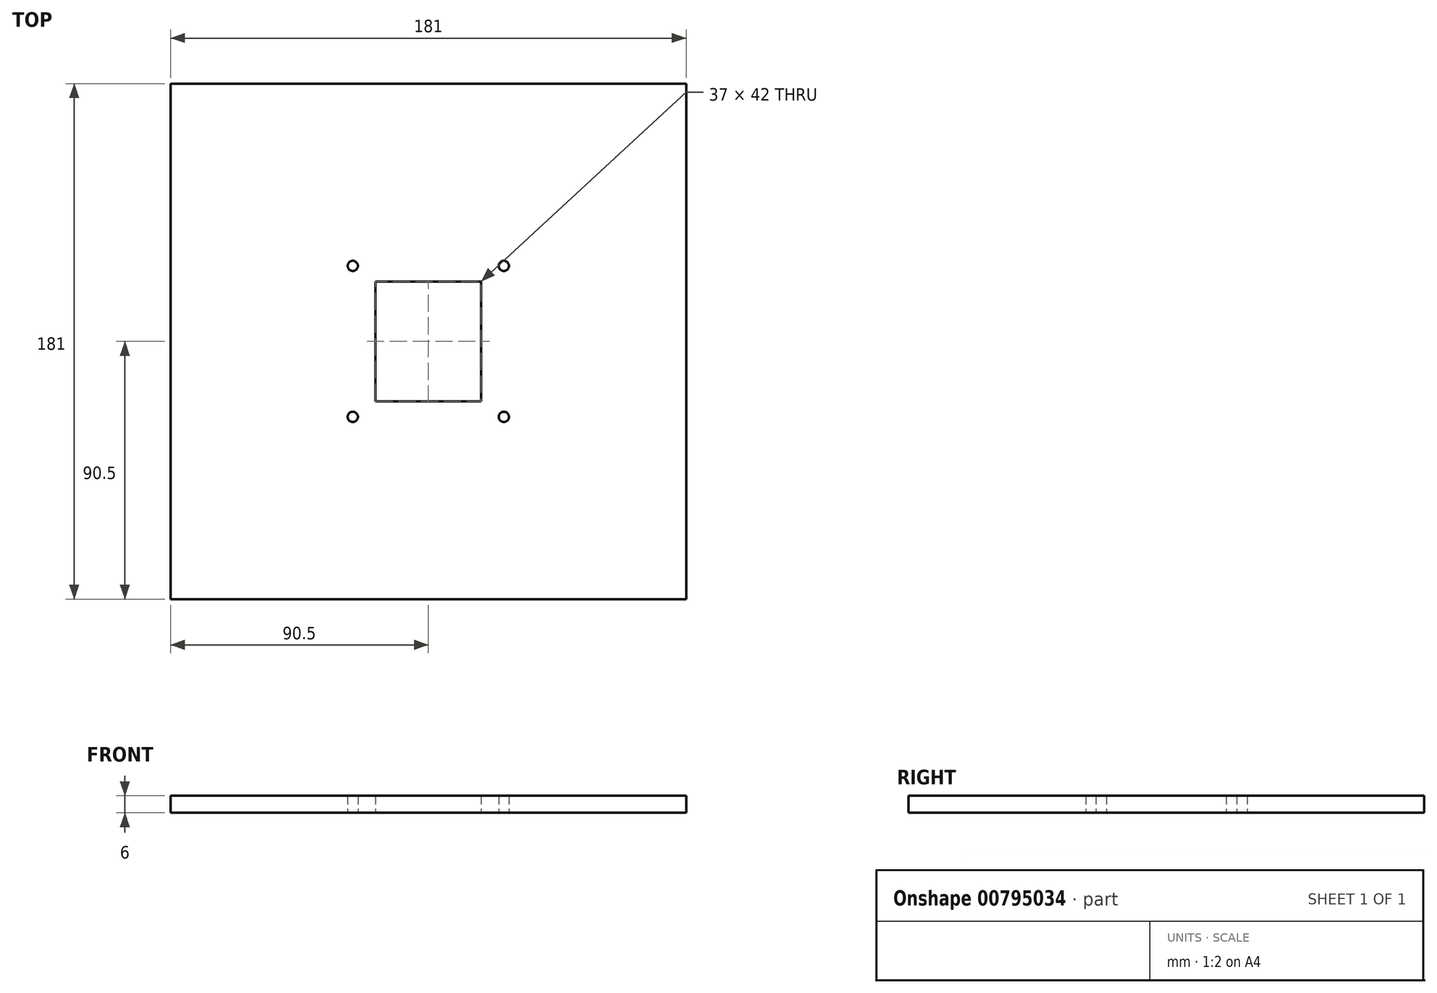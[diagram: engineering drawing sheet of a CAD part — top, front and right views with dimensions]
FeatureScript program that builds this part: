
annotation { "Feature Type Name" : "Feature", "Feature Type Description" : "" }
export const myFeature = defineFeature(function(context is Context, id is Id, definition is map)
    precondition{}
    {
        {
            var Q0;
            Q0=qCreatedBy(makeId("Top.planeOp"),FACE);
            var sketch = newSketch(context, id + "F0", { "sketchPlane" : qUnion([Q0])});
            skLineSegment(sketch, "E0.bottom", {"start": v(90.5, 90.5) * mm, "end": v(-90.5, 90.5) * mm});
            skLineSegment(sketch, "E0.top", {"start": v(90.5, -90.5) * mm, "end": v(-90.5, -90.5) * mm});
            skLineSegment(sketch, "E0.left", {"start": v(90.5, 90.5) * mm, "end": v(90.5, -90.5) * mm});
            skLineSegment(sketch, "E0.right", {"start": v(-90.5, 90.5) * mm, "end": v(-90.5, -90.5) * mm});
            skPoint(sketch, "E0.middle", {"position": v(0, 0) * mm});
            skLineSegment(sketch, "E1.bottom", {"start": v(-18.5, 21) * mm, "end": v(18.5, 21) * mm});
            skLineSegment(sketch, "E1.top", {"start": v(-18.5, -21) * mm, "end": v(18.5, -21) * mm});
            skLineSegment(sketch, "E1.left", {"start": v(-18.5, 21) * mm, "end": v(-18.5, -21) * mm});
            skLineSegment(sketch, "E1.right", {"start": v(18.5, 21) * mm, "end": v(18.5, -21) * mm});
            skCircle(sketch, "E2", {"center": v(-26.5, 26.5) * mm, "radius": 1.8 * mm});
            skCircle(sketch, "E3.0.1.0", {"center": v(-26.5, -26.5) * mm, "radius": 1.8 * mm});
            skCircle(sketch, "E3.1.0.0", {"center": v(26.5, 26.5) * mm, "radius": 1.8 * mm});
            skCircle(sketch, "E3.1.1.0", {"center": v(26.5, -26.5) * mm, "radius": 1.8 * mm});
            skLineSegment(sketch, "E3.direction1", {"start": v(-26.5, 26.5) * mm, "end": v(26.5, 26.5) * mm, "construction": true});
            skLineSegment(sketch, "E3.direction2", {"start": v(-26.5, 26.5) * mm, "end": v(-26.5, -26.5) * mm, "construction": true});
            skSolve(sketch);
        }
        {
            var Q0;
            Q0=makeQuery(id+"F0.imprint","IMPRINT",FACE,{"disambiguationData":[TD([[makeQuery(id+"F0.imprint","IMPRINT",EDGE,{"derivedFrom":sQuery(id+"F0.wireOp",EDGE,"E0.bottom")}),1.0]])]});
            extrude(context, id + "F1", {"entities" : qUnion([Q0]), "depth" : 6 * mm, "offsetDistance" : 25 * mm});
        }
    });
